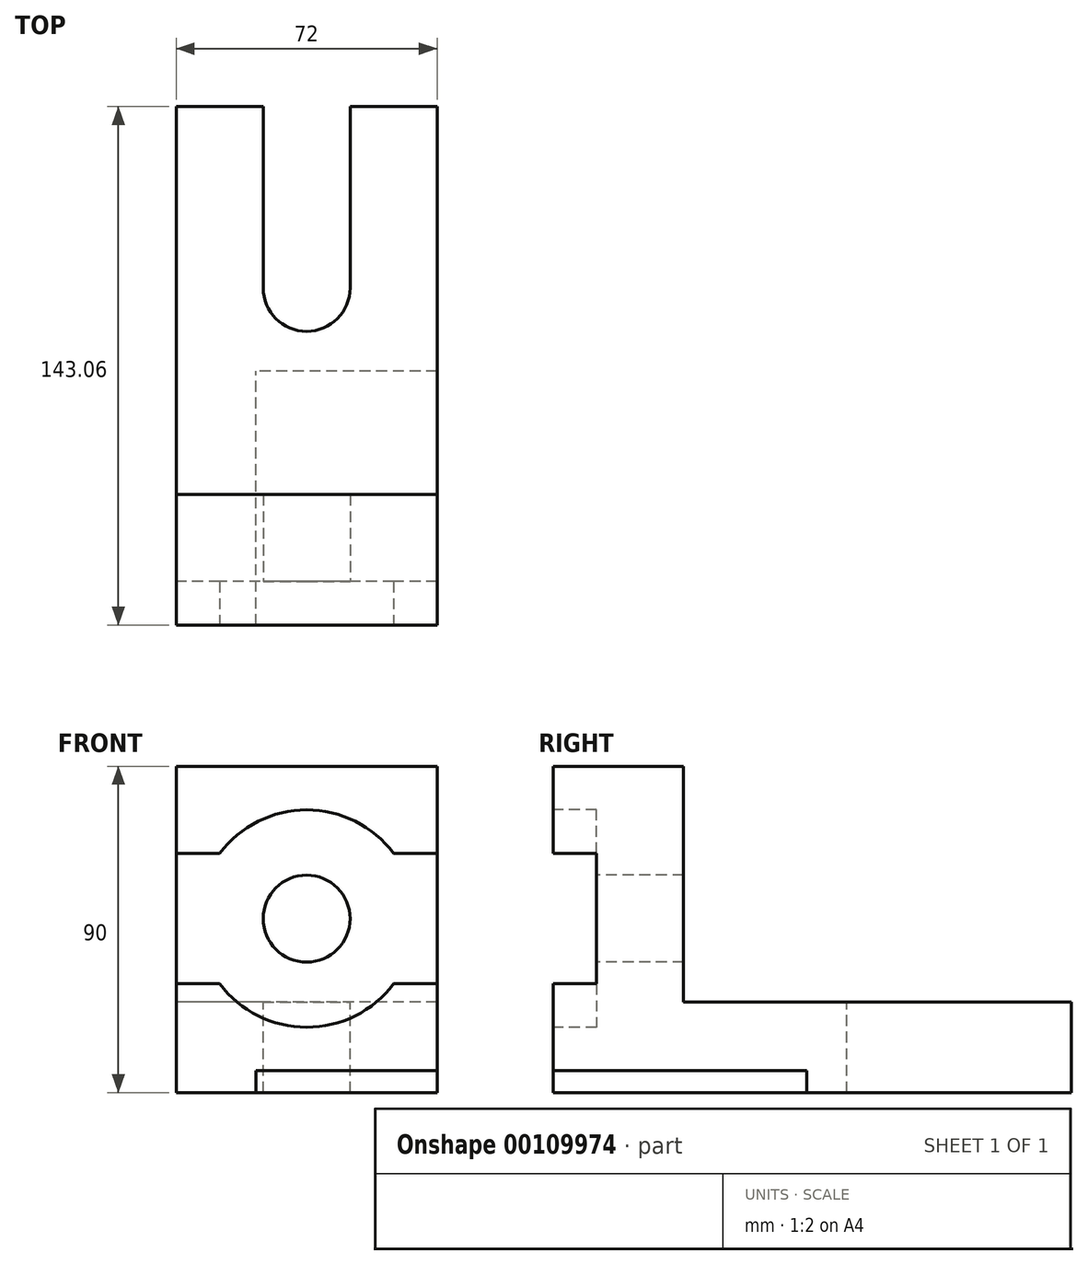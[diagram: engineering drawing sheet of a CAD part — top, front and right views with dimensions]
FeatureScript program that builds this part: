
annotation { "Feature Type Name" : "Feature", "Feature Type Description" : "" }
export const myFeature = defineFeature(function(context is Context, id is Id, definition is map)
    precondition{}
    {
        {
            var Q0;
            Q0=qCreatedBy(makeId("Right.planeOp"),FACE);
            var sketch = newSketch(context, id + "F0", { "sketchPlane" : qUnion([Q0])});
            skLineSegment(sketch, "E0", {"start": v(-90.16, 45.64) * mm, "end": v(-54.16, 45.64) * mm});
            skLineSegment(sketch, "E1", {"start": v(-54.16, 45.64) * mm, "end": v(-54.16, -19.36) * mm});
            skLineSegment(sketch, "E2", {"start": v(-54.16, -19.36) * mm, "end": v(52.9, -19.36) * mm});
            skLineSegment(sketch, "E3", {"start": v(52.9, -19.36) * mm, "end": v(52.9, -44.36) * mm});
            skLineSegment(sketch, "E4", {"start": v(52.9, -44.36) * mm, "end": v(-20.1, -44.36) * mm});
            skLineSegment(sketch, "E5", {"start": v(-20.1, -44.36) * mm, "end": v(-20.1, -38.36) * mm});
            skLineSegment(sketch, "E6", {"start": v(-20.1, -38.36) * mm, "end": v(-90.16, -38.36) * mm});
            skLineSegment(sketch, "E7", {"start": v(-90.16, 45.64) * mm, "end": v(-90.16, -38.36) * mm});
            skSolve(sketch);
        }
        {
            var Q0;
            Q0 = qSketchRegion(id + "F0", true);
            extrude(context, id + "F1", {"entities" : qUnion([Q0]), "endBound" : BoundingType.SYMMETRIC, "depth" : 72 * mm});
        }
        {
            var Q0;
            Q0=makeQuery(id+"F1.opExtrude","SWEPT_FACE",FACE,{"disambiguationData":[OSD([sQuery(id+"F0.wireOp",EDGE,"E6")])]});
            var sketch = newSketch(context, id + "F2", { "sketchPlane" : qUnion([Q0])});
            skLineSegment(sketch, "E8.bottom", {"start": v(-36, 90.16) * mm, "end": v(-14, 90.16) * mm});
            skLineSegment(sketch, "E8.top", {"start": v(-36, 20.1) * mm, "end": v(-14, 20.1) * mm});
            skLineSegment(sketch, "E8.left", {"start": v(-36, 90.16) * mm, "end": v(-36, 20.1) * mm});
            skLineSegment(sketch, "E8.right", {"start": v(-14, 90.16) * mm, "end": v(-14, 20.1) * mm});
            skSolve(sketch);
        }
        {
            var Q0;
            Q0 = qSketchRegion(id + "F2", true);
            extrude(context, id + "F3", {"entities" : qUnion([Q0]), "operationType" : NewBodyOperationType.ADD, "depth" : 6 * mm});
        }
        {
            var Q0;
            Q0=makeQuery(id+"F3.boolean.opBoolean","MERGE",FACE,{"derivedFrom":[makeQuery(id+"F1.opExtrude","SWEPT_FACE",FACE,{"disambiguationData":[OSD([sQuery(id+"F0.wireOp",EDGE,"E7")])]}),makeQuery(id+"F3.opExtrude","SWEPT_FACE",FACE,{"disambiguationData":[OSD([sQuery(id+"F2.wireOp",EDGE,"E8.bottom")])]})]});
            var sketch = newSketch(context, id + "F4", { "sketchPlane" : qUnion([Q0])});
            skCircle(sketch, "E9", {"center": v(0, 3.64) * mm, "radius": 12 * mm});
            skSolve(sketch);
        }
        {
            var Q0;
            Q0 = qSketchRegion(id + "F4", true);
            extrude(context, id + "F5", {"entities" : qUnion([Q0]), "operationType" : NewBodyOperationType.REMOVE, "endBound" : BoundingType.THROUGH_ALL, "oppositeDirection" : true, "depth" : 25 * mm});
        }
        {
            var Q0;
            Q0=makeQuery(id+"F3.boolean.opBoolean","MERGE",FACE,{"derivedFrom":[makeQuery(id+"F1.opExtrude","SWEPT_FACE",FACE,{"disambiguationData":[OSD([sQuery(id+"F0.wireOp",EDGE,"E7")])]}),makeQuery(id+"F3.opExtrude","SWEPT_FACE",FACE,{"disambiguationData":[OSD([sQuery(id+"F2.wireOp",EDGE,"E8.bottom")])]})]});
            var sketch = newSketch(context, id + "F6", { "sketchPlane" : qUnion([Q0])});
            skCircle(sketch, "E10", {"center": v(0, 3.64) * mm, "radius": 30 * mm});
            skSolve(sketch);
        }
        {
            var Q0;
            Q0 = qSketchRegion(id + "F6", true);
            extrude(context, id + "F7", {"entities" : qUnion([Q0]), "operationType" : NewBodyOperationType.REMOVE, "oppositeDirection" : true, "depth" : 12 * mm});
        }
        {
            var Q0;
            Q0=makeQuery(id+"F1.opExtrude","CAP_FACE",FACE,{"disambiguationData":[OSD([sQuery(id+"F0.wireOp",EDGE,"E0"),sQuery(id+"F0.wireOp",EDGE,"E1"),sQuery(id+"F0.wireOp",EDGE,"E2"),sQuery(id+"F0.wireOp",EDGE,"E3"),sQuery(id+"F0.wireOp",EDGE,"E4"),sQuery(id+"F0.wireOp",EDGE,"E5"),sQuery(id+"F0.wireOp",EDGE,"E6"),sQuery(id+"F0.wireOp",EDGE,"E7")])],"isStart":false});
            var sketch = newSketch(context, id + "F8", { "sketchPlane" : qUnion([Q0])});
            skLineSegment(sketch, "E11.bottom", {"start": v(-90.16, 21.64) * mm, "end": v(-78.16, 21.64) * mm});
            skLineSegment(sketch, "E11.top", {"start": v(-90.16, -14.36) * mm, "end": v(-78.16, -14.36) * mm});
            skLineSegment(sketch, "E11.left", {"start": v(-90.16, 21.64) * mm, "end": v(-90.16, -14.36) * mm});
            skLineSegment(sketch, "E11.right", {"start": v(-78.16, 21.64) * mm, "end": v(-78.16, -14.36) * mm});
            skSolve(sketch);
        }
        {
            var Q0;
            Q0=makeQuery(id+"F3.boolean.opBoolean","MERGE",FACE,{"derivedFrom":[makeQuery(id+"F1.opExtrude","CAP_FACE",FACE,{"disambiguationData":[OSD([sQuery(id+"F0.wireOp",EDGE,"E0"),sQuery(id+"F0.wireOp",EDGE,"E1"),sQuery(id+"F0.wireOp",EDGE,"E2"),sQuery(id+"F0.wireOp",EDGE,"E3"),sQuery(id+"F0.wireOp",EDGE,"E4"),sQuery(id+"F0.wireOp",EDGE,"E5"),sQuery(id+"F0.wireOp",EDGE,"E6"),sQuery(id+"F0.wireOp",EDGE,"E7")])],"isStart":true}),makeQuery(id+"F3.opExtrude","SWEPT_FACE",FACE,{"disambiguationData":[OSD([sQuery(id+"F2.wireOp",EDGE,"E8.left")])]})]});
            var sketch = newSketch(context, id + "F9", { "sketchPlane" : qUnion([Q0])});
            skLineSegment(sketch, "E12.bottom", {"start": v(90.16, 21.64) * mm, "end": v(78.16, 21.64) * mm});
            skLineSegment(sketch, "E12.top", {"start": v(90.16, -14.36) * mm, "end": v(78.16, -14.36) * mm});
            skLineSegment(sketch, "E12.left", {"start": v(90.16, 21.64) * mm, "end": v(90.16, -14.36) * mm});
            skLineSegment(sketch, "E12.right", {"start": v(78.16, 21.64) * mm, "end": v(78.16, -14.36) * mm});
            skSolve(sketch);
        }
        {
            var Q1;
            Q1=makeQuery(id+"F8.imprint","IMPRINT",FACE,{"disambiguationData":[TD([[makeQuery(id+"F8.imprint","IMPRINT",EDGE,{"derivedFrom":sQuery(id+"F8.wireOp",EDGE,"E11.bottom")}),-1.0]])]});
            var Q2;
            Q2=makeQuery(id+"F9.imprint","IMPRINT",FACE,{"disambiguationData":[TD([[makeQuery(id+"F9.imprint","IMPRINT",EDGE,{"derivedFrom":sQuery(id+"F9.wireOp",EDGE,"E12.bottom")}),1.0]])]});
            loft(context, id + "F10", {"operationType" : NewBodyOperationType.REMOVE, "sheetProfilesArray" : [{ "sheetProfileEntities" : qUnion([Q1]) }, { "sheetProfileEntities" : qUnion([Q2]) }]});
        }
        {
            var Q0;
            Q0=makeQuery(id+"F1.opExtrude","SWEPT_FACE",FACE,{"disambiguationData":[OSD([sQuery(id+"F0.wireOp",EDGE,"E2")])]});
            var sketch = newSketch(context, id + "F11", { "sketchPlane" : qUnion([Q0])});
            skLineSegment(sketch, "E13.bottom", {"start": v(12, 52.9) * mm, "end": v(-12, 52.9) * mm});
            skLineSegment(sketch, "E13.left", {"start": v(12, 52.9) * mm, "end": v(12, 2.9) * mm});
            skLineSegment(sketch, "E13.right", {"start": v(-12, 52.9) * mm, "end": v(-12, 2.9) * mm});
            skArc(sketch, "E14", {"start": v(-12, 2.9) * mm, "mid": v(0, -9.1) * mm, "end": v(12, 2.9) * mm});
            skSolve(sketch);
        }
        {
            var Q0;
            Q0 = qSketchRegion(id + "F11", true);
            extrude(context, id + "F12", {"entities" : qUnion([Q0]), "operationType" : NewBodyOperationType.REMOVE, "oppositeDirection" : true, "depth" : 25 * mm});
        }
    });
